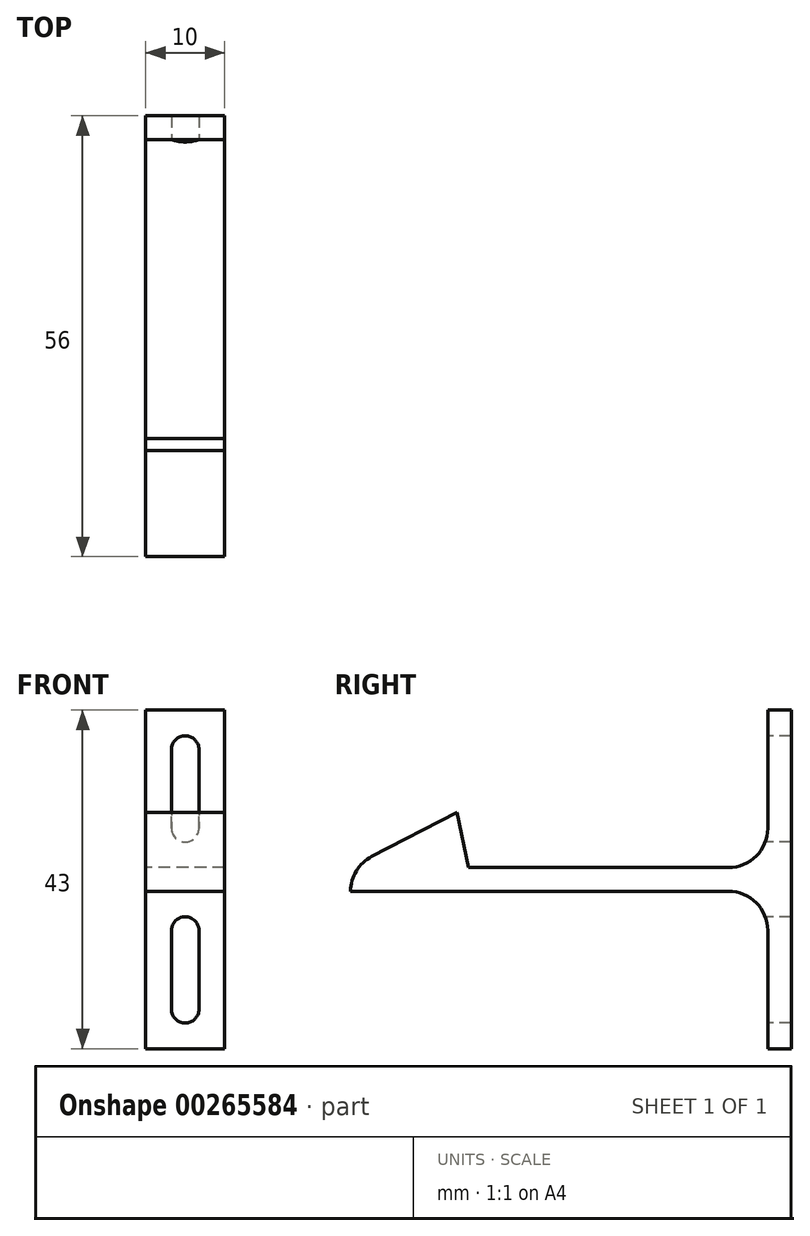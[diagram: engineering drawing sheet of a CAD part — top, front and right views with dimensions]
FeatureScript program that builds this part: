
annotation { "Feature Type Name" : "Feature", "Feature Type Description" : "" }
export const myFeature = defineFeature(function(context is Context, id is Id, definition is map)
    precondition{}
    {
        {
            var Q0;
            Q0=qCreatedBy(makeId("Right.planeOp"),FACE);
            var sketch = newSketch(context, id + "F0", { "sketchPlane" : qUnion([Q0])});
            skLineSegment(sketch, "E0", {"start": v(0, 0) * mm, "end": v(-38, 0) * mm});
            skLineSegment(sketch, "E1", {"start": v(-38, 0) * mm, "end": v(-39.5, 7) * mm});
            skLineSegment(sketch, "E2", {"start": v(-39.5, 7) * mm, "end": v(-53, 0) * mm});
            skLineSegment(sketch, "E3", {"start": v(-53, 0) * mm, "end": v(-53, -3) * mm});
            skLineSegment(sketch, "E4", {"start": v(-53, -3) * mm, "end": v(0, -3) * mm});
            skLineSegment(sketch, "E5", {"start": v(0, 0) * mm, "end": v(0, 20) * mm});
            skLineSegment(sketch, "E6", {"start": v(0, 20) * mm, "end": v(3, 20) * mm});
            skLineSegment(sketch, "E7", {"start": v(3, 20) * mm, "end": v(3, -23) * mm});
            skLineSegment(sketch, "E8", {"start": v(3, -23) * mm, "end": v(0, -23) * mm});
            skLineSegment(sketch, "E9", {"start": v(0, -23) * mm, "end": v(0, -3) * mm});
            skSolve(sketch);
        }
        {
            var Q0;
            Q0=makeQuery(id+"F0.imprint","IMPRINT",FACE,{"disambiguationData":[TD([[makeQuery(id+"F0.imprint","IMPRINT",EDGE,{"derivedFrom":sQuery(id+"F0.wireOp",EDGE,"E0")}),1.0]])]});
            extrude(context, id + "F1", {"entities" : qUnion([Q0]), "endBound" : BoundingType.SYMMETRIC, "depth" : 10 * mm});
        }
        {
            var Q0;
            Q0=makeQuery(id+"F1.opExtrude","SWEPT_FACE",FACE,{"disambiguationData":[OSD([sQuery(id+"F0.wireOp",EDGE,"E5")])]});
            var sketch = newSketch(context, id + "F2", { "sketchPlane" : qUnion([Q0])});
            skLineSegment(sketch, "E10", {"start": v(-5, 10) * mm, "end": v(0, 10) * mm, "construction": true});
            skLineSegment(sketch, "E11", {"start": v(0, 0) * mm, "end": v(0, 10) * mm, "construction": true});
            skCircle(sketch, "E12", {"center": v(0, 15) * mm, "radius": 1.75 * mm});
            skLineSegment(sketch, "E13", {"start": v(0, 10) * mm, "end": v(0, 20) * mm, "construction": true});
            skLineSegment(sketch, "E14", {"start": v(0, 10) * mm, "end": v(5, 10) * mm, "construction": true});
            skCircle(sketch, "E15", {"center": v(0, 5) * mm, "radius": 1.75 * mm});
            skLineSegment(sketch, "E16", {"start": v(0, 5) * mm, "end": v(-1.75, 5) * mm});
            skLineSegment(sketch, "E17", {"start": v(-1.75, 5) * mm, "end": v(-1.75, 15) * mm});
            skLineSegment(sketch, "E18", {"start": v(0, 5) * mm, "end": v(1.75, 5) * mm});
            skLineSegment(sketch, "E19", {"start": v(1.75, 5) * mm, "end": v(1.75, 15) * mm});
            skSolve(sketch);
        }
        {
            var Q0;
            {var subQ0=sQuery(id+"F2.wireOp",EDGE,"E12");var subQ1=makeQuery(id+"F2.imprint","INTERSECT",VERTEX,{"derivedFrom":[subQ0,sQuery(id+"F2.wireOp",EDGE,"E17")]});Q0=makeQuery(id+"F2.imprint","IMPRINT",FACE,{"disambiguationData":[TD([[makeQuery(id+"F2.imprint","IMPRINT",EDGE,{"disambiguationData":[TD([[subQ1,1.0]])],"derivedFrom":subQ0}),1.0]])]});}
            var Q1;
            {var subQ0=sQuery(id+"F2.wireOp",EDGE,"E17");Q1=makeQuery(id+"F2.imprint","IMPRINT",FACE,{"disambiguationData":[TD([[makeQuery(id+"F2.imprint","IMPRINT",EDGE,{"derivedFrom":subQ0}),-1.0]])]});}
            var Q2;
            {var subQ0=sQuery(id+"F2.wireOp",EDGE,"E16");Q2=makeQuery(id+"F2.imprint","IMPRINT",FACE,{"disambiguationData":[TD([[makeQuery(id+"F2.imprint","IMPRINT",EDGE,{"derivedFrom":subQ0}),-1.0]])]});}
            var Q3;
            {var subQ0=sQuery(id+"F2.wireOp",EDGE,"E16");Q3=makeQuery(id+"F2.imprint","IMPRINT",FACE,{"disambiguationData":[TD([[makeQuery(id+"F2.imprint","IMPRINT",EDGE,{"derivedFrom":subQ0}),1.0]])]});}
            extrude(context, id + "F3", {"entities" : qUnion([Q0, Q1, Q2, Q3]), "operationType" : NewBodyOperationType.REMOVE, "endBound" : BoundingType.THROUGH_ALL, "oppositeDirection" : true, "depth" : 25 * mm});
        }
        {
            var Q0;
            Q0=makeQuery(id+"F1.opExtrude","SWEPT_FACE",FACE,{"disambiguationData":[OSD([sQuery(id+"F0.wireOp",EDGE,"E9")])]});
            var sketch = newSketch(context, id + "F4", { "sketchPlane" : qUnion([Q0])});
            skLineSegment(sketch, "E20", {"start": v(0, -3) * mm, "end": v(0, -13) * mm, "construction": true});
            skLineSegment(sketch, "E21", {"start": v(-5, -13) * mm, "end": v(0, -13) * mm, "construction": true});
            skLineSegment(sketch, "E22", {"start": v(0, -13) * mm, "end": v(0, -23) * mm, "construction": true});
            skLineSegment(sketch, "E23", {"start": v(0, -13) * mm, "end": v(5, -13) * mm, "construction": true});
            skCircle(sketch, "E24", {"center": v(0, -8) * mm, "radius": 1.75 * mm});
            skCircle(sketch, "E25", {"center": v(0, -18) * mm, "radius": 1.75 * mm});
            skLineSegment(sketch, "E26", {"start": v(0, -8) * mm, "end": v(-1.75, -8) * mm, "construction": true});
            skLineSegment(sketch, "E27", {"start": v(-1.75, -8) * mm, "end": v(-1.75, -18) * mm});
            skLineSegment(sketch, "E28", {"start": v(-1.75, -18) * mm, "end": v(1.75, -18) * mm, "construction": true});
            skLineSegment(sketch, "E29", {"start": v(1.75, -18) * mm, "end": v(1.75, -8) * mm});
            skSolve(sketch);
        }
        {
            var Q0;
            {var subQ0=sQuery(id+"F4.wireOp",EDGE,"E25");var subQ1=makeQuery(id+"F4.imprint","INTERSECT",VERTEX,{"derivedFrom":[subQ0,sQuery(id+"F4.wireOp",EDGE,"E27")]});Q0=makeQuery(id+"F4.imprint","IMPRINT",FACE,{"disambiguationData":[TD([[makeQuery(id+"F4.imprint","IMPRINT",EDGE,{"disambiguationData":[TD([[subQ1,1.0]])],"derivedFrom":subQ0}),1.0]])]});}
            var Q1;
            {var subQ0=sQuery(id+"F4.wireOp",EDGE,"E27");Q1=makeQuery(id+"F4.imprint","IMPRINT",FACE,{"disambiguationData":[TD([[makeQuery(id+"F4.imprint","IMPRINT",EDGE,{"derivedFrom":subQ0}),1.0]])]});}
            var Q2;
            {var subQ0=sQuery(id+"F4.wireOp",EDGE,"E24");var subQ1=makeQuery(id+"F4.imprint","INTERSECT",VERTEX,{"derivedFrom":[subQ0,sQuery(id+"F4.wireOp",EDGE,"E27")]});Q2=makeQuery(id+"F4.imprint","IMPRINT",FACE,{"disambiguationData":[TD([[makeQuery(id+"F4.imprint","IMPRINT",EDGE,{"disambiguationData":[TD([[subQ1,1.0]])],"derivedFrom":subQ0}),1.0]])]});}
            extrude(context, id + "F5", {"entities" : qUnion([Q0, Q1, Q2]), "operationType" : NewBodyOperationType.REMOVE, "oppositeDirection" : true, "depth" : 25 * mm});
        }
        {
            var Q0;
            Q0=makeQuery(id+"F1.opExtrude","SWEPT_EDGE",EDGE,{"disambiguationData":[OSD([sQuery(id+"F0.wireOp",EDGE,"E0"),sQuery(id+"F0.wireOp",EDGE,"E5")])]});
            fillet(context, id + "F6", {"entities" : qUnion([Q0]), "radius" : 5 * mm, "tangentPropagation" : true, "allowEdgeOverflow" : false});
        }
        {
            var Q0;
            Q0=makeQuery(id+"F1.opExtrude","SWEPT_EDGE",EDGE,{"disambiguationData":[OSD([sQuery(id+"F0.wireOp",EDGE,"E4"),sQuery(id+"F0.wireOp",EDGE,"E9")])]});
            fillet(context, id + "F7", {"entities" : qUnion([Q0]), "radius" : 5 * mm, "tangentPropagation" : true, "allowEdgeOverflow" : false});
        }
        {
            var Q0;
            Q0=makeQuery(id+"F1.opExtrude","SWEPT_EDGE",EDGE,{"disambiguationData":[OSD([sQuery(id+"F0.wireOp",EDGE,"E2"),sQuery(id+"F0.wireOp",EDGE,"E3")])]});
            fillet(context, id + "F8", {"entities" : qUnion([Q0]), "radius" : 5 * mm, "tangentPropagation" : true, "allowEdgeOverflow" : false});
        }
    });
